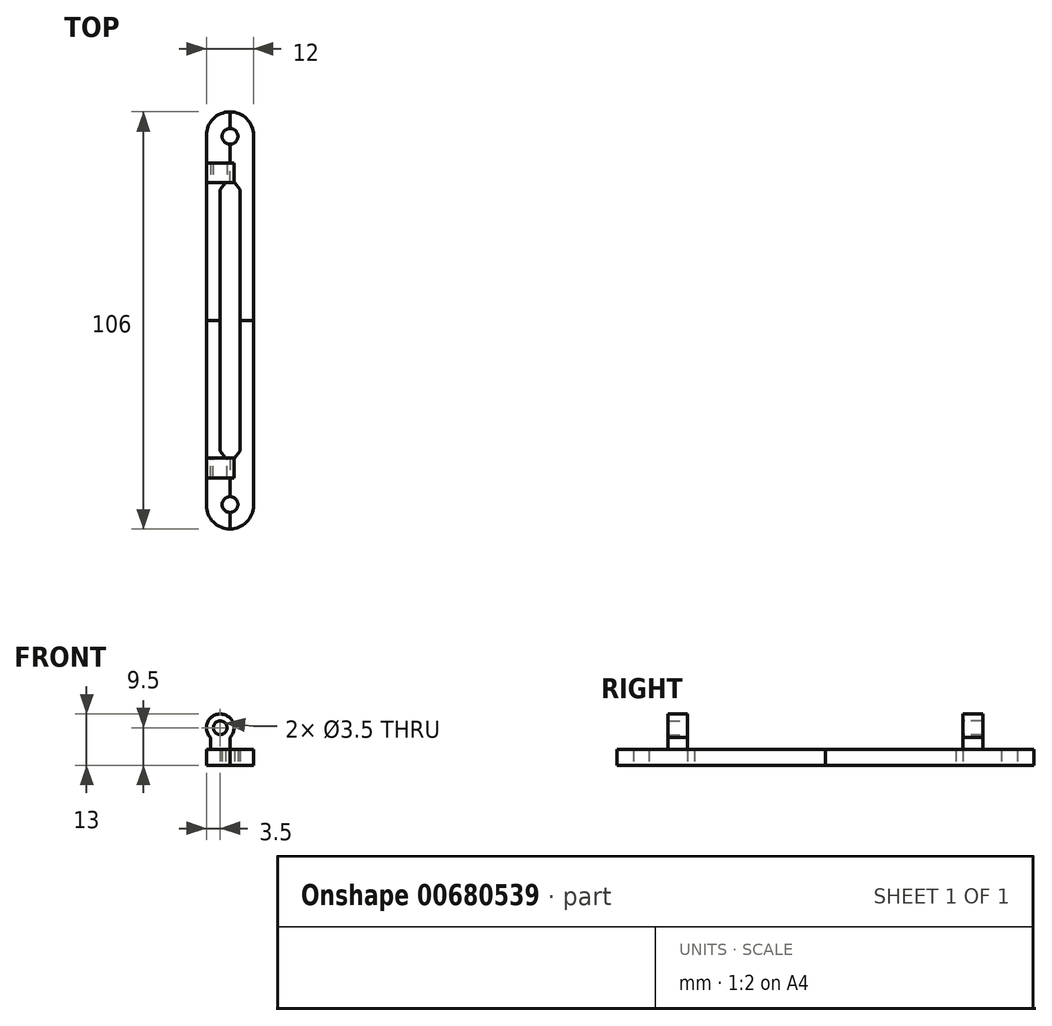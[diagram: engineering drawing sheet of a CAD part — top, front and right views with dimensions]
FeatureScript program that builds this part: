
annotation { "Feature Type Name" : "Feature", "Feature Type Description" : "" }
export const myFeature = defineFeature(function(context is Context, id is Id, definition is map)
    precondition{}
    {
        {
            var Q0;
            Q0=qCreatedBy(makeId("Top.planeOp"),FACE);
            var sketch = newSketch(context, id + "F0", { "sketchPlane" : qUnion([Q0])});
            skLineSegment(sketch, "E0", {"start": v(-2.5, 0) * mm, "end": v(-2.5, 33.22) * mm});
            skLineSegment(sketch, "E1", {"start": v(-2.5, 33.22) * mm, "end": v(-1.16, 35) * mm});
            skLineSegment(sketch, "E2", {"start": v(-1.16, 35) * mm, "end": v(0, 35) * mm});
            skLineSegment(sketch, "E3", {"start": v(0, 35) * mm, "end": v(0, 53) * mm});
            skLineSegment(sketch, "E4", {"start": v(0, 53) * mm, "end": v(-6, 53) * mm});
            skLineSegment(sketch, "E5", {"start": v(-6, 53) * mm, "end": v(-6, 0) * mm});
            skLineSegment(sketch, "E6", {"start": v(-6, 0) * mm, "end": v(-2.5, 0) * mm});
            skCircle(sketch, "E7", {"center": v(0, 46.77) * mm, "radius": 2 * mm});
            skSolve(sketch);
        }
        {
            var Q0;
            Q0=makeQuery(id+"F0.imprint","IMPRINT",FACE,{"disambiguationData":[TD([[makeQuery(id+"F0.imprint","IMPRINT",EDGE,{"derivedFrom":sQuery(id+"F0.wireOp",EDGE,"E0")}),1.0]])]});
            extrude(context, id + "F1", {"entities" : qUnion([Q0]), "depth" : 4 * mm, "offsetDistance" : 25 * mm});
        }
        {
            var Q0;
            Q0=qCreatedBy(makeId("Front.planeOp"),FACE);
            var sketch = newSketch(context, id + "F2", { "sketchPlane" : qUnion([Q0])});
            skLineSegment(sketch, "E8.bottom", {"start": v(0, 4) * mm, "end": v(-5, 4) * mm});
            skLineSegment(sketch, "E8.top", {"start": v(0, 12) * mm, "end": v(-5, 12) * mm});
            skLineSegment(sketch, "E8.left", {"start": v(0, 4) * mm, "end": v(0, 12) * mm});
            skLineSegment(sketch, "E8.right", {"start": v(-5, 4) * mm, "end": v(-5, 12) * mm});
            skCircle(sketch, "E9", {"center": v(-2.5, 9.5) * mm, "radius": 1.75 * mm});
            skLineSegment(sketch, "E10", {"start": v(-2.5, 12) * mm, "end": v(-2.5, 4) * mm, "construction": true});
            skCircle(sketch, "E11", {"center": v(-2.5, 9.5) * mm, "radius": 3.5 * mm});
            skSolve(sketch);
        }
        {
            var Q0;
            Q0=makeQuery(id+"F2.imprint","IMPRINT",FACE,{"disambiguationData":[TD([[makeQuery(id+"F2.imprint","IMPRINT",EDGE,{"derivedFrom":sQuery(id+"F2.wireOp",EDGE,"E9")}),-1.0]])]});
            var Q1;
            {var subQ0=sQuery(id+"F2.wireOp",EDGE,"E8.bottom");Q1=makeQuery(id+"F2.imprint","IMPRINT",FACE,{"disambiguationData":[TD([[makeQuery(id+"F2.imprint","IMPRINT",EDGE,{"derivedFrom":subQ0}),-1.0]])]});}
            var Q2;
            {var subQ0=sQuery(id+"F2.wireOp",EDGE,"E11");var subQ1=sQuery(id+"F2.wireOp",EDGE,"E8.left");var subQ2=makeQuery(id+"F2.imprint","INTERSECT",VERTEX,{"disambiguationData":[OD(0.0)],"derivedFrom":[subQ1,subQ0]});Q2=makeQuery(id+"F2.imprint","IMPRINT",FACE,{"disambiguationData":[TD([[makeQuery(id+"F2.imprint","IMPRINT",EDGE,{"disambiguationData":[TD([[subQ2,-1.0]])],"derivedFrom":subQ1}),-1.0]])]});}
            var Q3;
            {var subQ0=sQuery(id+"F2.wireOp",EDGE,"E11");var subQ1=sQuery(id+"F2.wireOp",EDGE,"E8.top");var subQ2=makeQuery(id+"F2.imprint","INTERSECT",VERTEX,{"disambiguationData":[OD(0.0)],"derivedFrom":[subQ1,subQ0]});Q3=makeQuery(id+"F2.imprint","IMPRINT",FACE,{"disambiguationData":[TD([[makeQuery(id+"F2.imprint","IMPRINT",EDGE,{"disambiguationData":[TD([[subQ2,-1.0]])],"derivedFrom":subQ1}),-1.0]])]});}
            var Q4;
            {var subQ0=sQuery(id+"F2.wireOp",EDGE,"E11");var subQ1=sQuery(id+"F2.wireOp",EDGE,"E8.right");var subQ2=makeQuery(id+"F2.imprint","INTERSECT",VERTEX,{"disambiguationData":[OD(0.0)],"derivedFrom":[subQ1,subQ0]});Q4=makeQuery(id+"F2.imprint","IMPRINT",FACE,{"disambiguationData":[TD([[makeQuery(id+"F2.imprint","IMPRINT",EDGE,{"disambiguationData":[TD([[subQ2,-1.0]])],"derivedFrom":subQ1}),1.0]])]});}
            extrude(context, id + "F3", {"entities" : qUnion([Q0, Q1, Q2, Q3, Q4]), "oppositeDirection" : true, "depth" : 40 * mm, "offsetDistance" : 25 * mm, "hasSecondDirection" : true, "secondDirectionOppositeDirection" : false, "secondDirectionDepth" : -35 * mm});
        }
        {
            var Q0;
            Q0=makeQuery(id+"F1.opExtrude","SWEPT_BODY",BODY,{"disambiguationData":[OSD([sQuery(id+"F0.wireOp",EDGE,"E0"),sQuery(id+"F0.wireOp",EDGE,"E1"),sQuery(id+"F0.wireOp",EDGE,"E2"),sQuery(id+"F0.wireOp",EDGE,"E3"),sQuery(id+"F0.wireOp",EDGE,"E4"),sQuery(id+"F0.wireOp",EDGE,"E5"),sQuery(id+"F0.wireOp",EDGE,"E6"),sQuery(id+"F0.wireOp",EDGE,"E7")])]});
            var Q1;
            Q1=makeQuery(id+"F3.opExtrude","SWEPT_BODY",BODY,{"disambiguationData":[OSD([sQuery(id+"F2.wireOp",EDGE,"E8.bottom"),sQuery(id+"F2.wireOp",EDGE,"E8.left"),sQuery(id+"F2.wireOp",EDGE,"E8.right"),sQuery(id+"F2.wireOp",EDGE,"E9"),sQuery(id+"F2.wireOp",EDGE,"E11")])]});
            var Q2;
            Q2=makeQuery(id+"F1.opExtrude","SWEPT_FACE",FACE,{"disambiguationData":[OSD([sQuery(id+"F0.wireOp",EDGE,"E6")])]});
            mirror(context, id + "F4", {"entities" : qUnion([Q0, Q1]), "mirrorPlane" : qUnion([Q2])});
        }
        {
            var Q0;
            Q0=makeQuery(id+"F1.opExtrude","SWEPT_BODY",BODY,{"disambiguationData":[OSD([sQuery(id+"F0.wireOp",EDGE,"E0"),sQuery(id+"F0.wireOp",EDGE,"E1"),sQuery(id+"F0.wireOp",EDGE,"E2"),sQuery(id+"F0.wireOp",EDGE,"E3"),sQuery(id+"F0.wireOp",EDGE,"E4"),sQuery(id+"F0.wireOp",EDGE,"E5"),sQuery(id+"F0.wireOp",EDGE,"E6"),sQuery(id+"F0.wireOp",EDGE,"E7")])]});
            var Q1;
            Q1=makeQuery(id+"F4.opPattern","COPY",BODY,{"derivedFrom":makeQuery(id+"F1.opExtrude","SWEPT_BODY",BODY,{"disambiguationData":[OSD([sQuery(id+"F0.wireOp",EDGE,"E0"),sQuery(id+"F0.wireOp",EDGE,"E1"),sQuery(id+"F0.wireOp",EDGE,"E2"),sQuery(id+"F0.wireOp",EDGE,"E3"),sQuery(id+"F0.wireOp",EDGE,"E4"),sQuery(id+"F0.wireOp",EDGE,"E5"),sQuery(id+"F0.wireOp",EDGE,"E6"),sQuery(id+"F0.wireOp",EDGE,"E7")])]}),"instanceName":"1"});
            var Q2;
            {var subQ0=sQuery(id+"F0.wireOp",EDGE,"E3");Q2=makeQuery(id+"F4.opPattern","COPY",FACE,{"derivedFrom":makeQuery(id+"F1.opExtrude","SWEPT_FACE",FACE,{"disambiguationData":[OSD([subQ0]),TDD([makeQuery(id+"F0.imprint","IMPRINT",EDGE,{"disambiguationData":[TD([[makeQuery(id+"F0.imprint","INTERSECT",VERTEX,{"derivedFrom":[sQuery(id+"F0.wireOp",EDGE,"E2"),subQ0]}),-1.0]])],"derivedFrom":subQ0})])]}),"instanceName":"1"});}
            mirror(context, id + "F5", {"entities" : qUnion([Q0, Q1]), "mirrorPlane" : qUnion([Q2])});
        }
        {
            var Q0;
            Q0=makeQuery(id+"F5.opPattern","COPY",EDGE,{"derivedFrom":makeQuery(id+"F4.opPattern","COPY",EDGE,{"derivedFrom":makeQuery(id+"F1.opExtrude","SWEPT_EDGE",EDGE,{"disambiguationData":[OSD([sQuery(id+"F0.wireOp",EDGE,"E4"),sQuery(id+"F0.wireOp",EDGE,"E5")])]}),"instanceName":"1"}),"instanceName":"1"});
            var Q1;
            Q1=makeQuery(id+"F4.opPattern","COPY",EDGE,{"derivedFrom":makeQuery(id+"F1.opExtrude","SWEPT_EDGE",EDGE,{"disambiguationData":[OSD([sQuery(id+"F0.wireOp",EDGE,"E4"),sQuery(id+"F0.wireOp",EDGE,"E5")])]}),"instanceName":"1"});
            var Q2;
            Q2=makeQuery(id+"F5.opPattern","COPY",EDGE,{"derivedFrom":makeQuery(id+"F1.opExtrude","SWEPT_EDGE",EDGE,{"disambiguationData":[OSD([sQuery(id+"F0.wireOp",EDGE,"E4"),sQuery(id+"F0.wireOp",EDGE,"E5")])]}),"instanceName":"1"});
            var Q3;
            Q3=makeQuery(id+"F1.opExtrude","SWEPT_EDGE",EDGE,{"disambiguationData":[OSD([sQuery(id+"F0.wireOp",EDGE,"E4"),sQuery(id+"F0.wireOp",EDGE,"E5")])]});
            fillet(context, id + "F6", {"entities" : qUnion([Q0, Q1, Q2, Q3]), "radius" : 6 * mm, "tangentPropagation" : true, "allowEdgeOverflow" : false});
        }
    });
